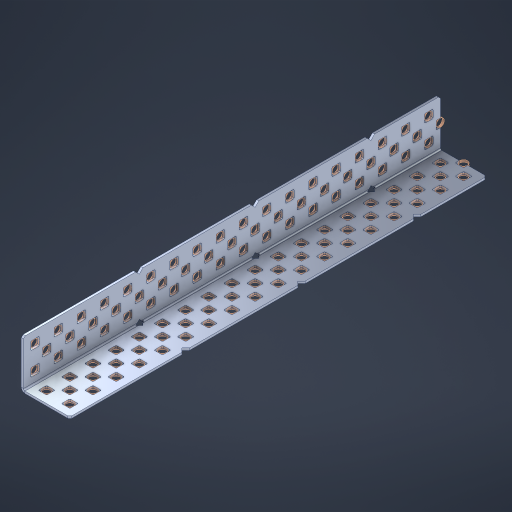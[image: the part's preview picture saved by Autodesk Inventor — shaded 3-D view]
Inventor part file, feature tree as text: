
AUTODESK INVENTOR PART (.ipt)
format: ipt  version: 2023 (Build 270158000, 158)  size: 1,412,096 bytes
history: native  units: in
note: dims shown in document units (in); Inventor stores cm internally (conversion verified against a paired STEP export)
features: other x114, extrude x106, sheet_metal_op x8, sketch x7, pattern_linear x2, mirror x1, chamfer x1
ambient origin geometry x8: Origin, YZ Plane, XZ Plane, XY Plane, X Axis, Y Axis, Z Axis, Center Point
bodies: Solid1 (feature_tree), Body (feature_tree)
feature tree (239):
  sheet_metal_op  "Flanges"
  sheet_metal_op  "Body Pattern"
  pattern_linear  "Center Pattern"  Spacing1=1.0in  [1 undecoded]
  other  "Arc Length"
  pattern_linear  "Notch Pattern"  Spacing1=0.1875in  [1 undecoded]
  other  "Diagonal Plane"
  mirror  "Everything Mirrored"
  chamfer  "End Chamfer"
  sketch  "Sketch1"  dims[d0=1.0in]
  other  "Plate1"
  sketch  "Sketch2"  dims[d1=9.0in]
  other  "Plate2"
  sheet_metal_op  "Bend1"
  sheet_metal_op  "Corner1"
  sketch  "Sketch8"  dims[d2=0.0469in]
  sketch  "Sketch9"  dims[d3=0.0469in]
  other  "Srf91"
  sheet_metal_op  "Body Pattern Sketch"
  other  "Srf92"
  sketch  "Sketch13"  dims[d4=0.0234in]
  sketch  "Sketch15"  dims[d5=0.0938in]
  sketch  "Sketch16"  dims[d6=0.0469in d7=1.0in d8=90.0deg d9=0.0312in d10=0.1875in d11=0.0469in d12=0.0469in d49=0.182in d50=0.02in d52=0.25in d53=0.0469in d54=0.0in d55=0.172in d56=1.0in d57=0.0in d60=7.0866in d62=0.5in d63=0.7874in d65=0.5in d85=0.1473in d86=0.1659in d89=0.0469in d90=0.0in d91=0.04in d92=0.0491in d95=2.5in d96=0.04in d97=0.25in d98=45.0deg d99=0.25in d106=0.182in d107=0.02in d108=0.5in d110=0.0469in d111=0.0in d112=0.172in d113=0.5in d114=0.0in d117=0.5in d123=0.25in d125=0.25in d126=0.0491in d127=0.1227in d128=0.08in d129=0.04in d130=2.5in]
  other  "Srf786"
  other  "Srf856"
  other  "Srf857"
  other  "Srf858"
  other  "Srf859"
  other  "Srf860"
  other  "Srf861"
  other  "Srf889"
  other  "Srf890"
  other  "Srf891"
  other  "Srf1275"
  other  "Srf1276"
  other  "Srf1278"
  other  "Srf1279"
  other  "Srf1280"
  other  "Srf1281"
  other  "Srf1282"
  other  "Srf1283"
  other  "Srf1277"
  other  "Srf1285"
  other  "Srf1286"
  other  "Srf1287"
  other  "Srf1383"
  other  "Srf1384"
  other  "Srf1385"
  other  "Srf1386"
  other  "Srf1387"
  other  "Srf1388"
  other  "Srf1389"
  other  "Srf1390"
  other  "Srf1391"
  other  "Srf1392"
  other  "Srf1393"
  other  "Srf1394"
  other  "Srf1395"
  other  "Srf1396"
  other  "Srf1397"
  other  "Srf1398"
  other  "Srf1399"
  other  "Srf1400"
  other  "Srf1401"
  other  "Srf1402"
  other  "Srf1403"
  other  "Srf1404"
  other  "Srf1405"
  other  "Srf1406"
  other  "Srf1407"
  other  "Srf1408"
  other  "Srf1409"
  other  "Srf1410"
  other  "Srf1445"
  other  "Srf1446"
  other  "Srf1447"
  other  "Srf1448"
  other  "Srf1449"
  other  "Srf1450"
  other  "Srf1451"
  other  "Srf1452"
  other  "Srf1453"
  other  "Srf1454"
  other  "Srf1455"
  other  "Srf1456"
  other  "Srf1457"
  other  "Srf1458"
  other  "Srf1475"
  other  "Srf1476"
  other  "Srf1477"
  other  "Srf1478"
  other  "Srf1479"
  other  "Srf1480"
  other  "Srf1481"
  other  "Srf1482"
  other  "Srf1483"
  other  "Srf1484"
  other  "Srf1485"
  other  "Srf1486"
  other  "Srf1487"
  other  "Srf1488"
  other  "Srf1489"
  other  "Srf1490"
  other  "Srf1491"
  other  "Srf1492"
  other  "Srf1493"
  other  "Srf1494"
  other  "Srf1495"
  other  "Srf1496"
  other  "Srf1497"
  other  "Srf1498"
  other  "Srf1499"
  other  "Srf1500"
  other  "Srf1501"
  other  "Srf1502"
  other  "Srf1537"
  other  "Srf1538"
  other  "Srf1539"
  other  "Srf1540"
  other  "Srf1541"
  other  "Srf1542"
  other  "Srf1543"
  other  "Srf1544"
  other  "Srf1545"
  other  "Srf1546"
  other  "Srf1547"
  other  "Srf1548"
  other  "Srf1549"
  other  "Srf1550"
  sheet_metal_op  "Body Stamp"
  sheet_metal_op  "Body Circle"
  other  "Center Stamp"
  other  "Center Circle"
  sheet_metal_op  "Notch"
  extrude  "ExtrusionSrf92"  Depth=0.0469in
  extrude  "ExtrusionSrf856"  Depth=0.0469in
  extrude  "ExtrusionSrf857"  Depth=0.182in
  extrude  "ExtrusionSrf858"  Depth=0.02in
  extrude  "ExtrusionSrf859"  Depth=0.25in
  extrude  "ExtrusionSrf860"  Depth=0.0469in
  extrude  "ExtrusionSrf861"  TaperAngle=0.0deg  [1 undecoded]
  extrude  "ExtrusionSrf889"  Depth=2.5in
  extrude  "ExtrusionSrf890"  Depth=1.0in TaperAngle=0.0deg
  extrude  "ExtrusionSrf891"  Depth=2.5in
  extrude  "ExtrusionSrf1275"  Depth=0.5in
  extrude  "ExtrusionSrf1276"  Depth=2.5in
  extrude  "ExtrusionSrf1277"  Depth=2.5in
  extrude  "ExtrusionSrf1278"  Depth=0.0469in
  extrude  "ExtrusionSrf1279"  Depth=2.5in TaperAngle=0.0deg
  extrude  "ExtrusionSrf1280"  Depth=2.5in
  extrude  "ExtrusionSrf1281"  Depth=0.25in TaperAngle=45.0deg
  extrude  "ExtrusionSrf1282"  Depth=0.25in
  extrude  "ExtrusionSrf1345"  Depth=0.182in
  extrude  "ExtrusionSrf1346"  Depth=0.02in
  extrude  "ExtrusionSrf1347"  Depth=0.5in
  extrude  "ExtrusionSrf1348"  Depth=0.0469in
  extrude  "ExtrusionSrf1383"  TaperAngle=0.0deg  [1 undecoded]
  extrude  "ExtrusionSrf1384"  Depth=2.5in
  extrude  "ExtrusionSrf1385"  Depth=0.5in TaperAngle=0.0deg
  extrude  "ExtrusionSrf1386"  Depth=0.5in
  extrude  "ExtrusionSrf1387"  Depth=0.25in
  extrude  "ExtrusionSrf1388"  Depth=0.25in
  extrude  "ExtrusionSrf1389"  Depth=2.5in
  extrude  "ExtrusionSrf1390"  Depth=2.5in
  extrude  "ExtrusionSrf1391"  Depth=2.5in
  extrude  "ExtrusionSrf1392"  Depth=2.5in
  extrude  "ExtrusionSrf1393"  Depth=2.5in
  extrude  "ExtrusionSrf1394"  [1 undecoded]
  extrude  "ExtrusionSrf1395"  [1 undecoded]
  extrude  "ExtrusionSrf1396"  [1 undecoded]
  extrude  "ExtrusionSrf1397"  [1 undecoded]
  extrude  "ExtrusionSrf1398"  [1 undecoded]
  extrude  "ExtrusionSrf1399"  [1 undecoded]
  extrude  "ExtrusionSrf1400"  [1 undecoded]
  extrude  "ExtrusionSrf1401"  [1 undecoded]
  extrude  "ExtrusionSrf1402"  [1 undecoded]
  extrude  "ExtrusionSrf1403"  [1 undecoded]
  extrude  "ExtrusionSrf1404"  [1 undecoded]
  extrude  "ExtrusionSrf1405"  [1 undecoded]
  extrude  "ExtrusionSrf1406"  [1 undecoded]
  extrude  "ExtrusionSrf1407"  [1 undecoded]
  extrude  "ExtrusionSrf1408"  [1 undecoded]
  extrude  "ExtrusionSrf1409"  [1 undecoded]
  extrude  "ExtrusionSrf1410"  [1 undecoded]
  extrude  "ExtrusionSrf1445"  [1 undecoded]
  extrude  "ExtrusionSrf1446"  [1 undecoded]
  extrude  "ExtrusionSrf1447"  [1 undecoded]
  extrude  "ExtrusionSrf1448"  [1 undecoded]
  extrude  "ExtrusionSrf1449"  [1 undecoded]
  extrude  "ExtrusionSrf1450"  [1 undecoded]
  extrude  "ExtrusionSrf1451"  [1 undecoded]
  extrude  "ExtrusionSrf1452"  [1 undecoded]
  extrude  "ExtrusionSrf1453"  [1 undecoded]
  extrude  "ExtrusionSrf1454"  [1 undecoded]
  extrude  "ExtrusionSrf1455"  [1 undecoded]
  extrude  "ExtrusionSrf1456"  [1 undecoded]
  extrude  "ExtrusionSrf1457"  [1 undecoded]
  extrude  "ExtrusionSrf1458"  [1 undecoded]
  extrude  "ExtrusionSrf1475"  [1 undecoded]
  extrude  "ExtrusionSrf1476"  [1 undecoded]
  extrude  "ExtrusionSrf1477"  [1 undecoded]
  extrude  "ExtrusionSrf1478"  [1 undecoded]
  extrude  "ExtrusionSrf1479"  [1 undecoded]
  extrude  "ExtrusionSrf1480"  [1 undecoded]
  extrude  "ExtrusionSrf1481"  [1 undecoded]
  extrude  "ExtrusionSrf1482"  [1 undecoded]
  extrude  "ExtrusionSrf1483"  [1 undecoded]
  extrude  "ExtrusionSrf1484"  [1 undecoded]
  extrude  "ExtrusionSrf1485"  [1 undecoded]
  extrude  "ExtrusionSrf1486"  [1 undecoded]
  extrude  "ExtrusionSrf1487"  [1 undecoded]
  extrude  "ExtrusionSrf1488"  [1 undecoded]
  extrude  "ExtrusionSrf1489"  [1 undecoded]
  extrude  "ExtrusionSrf1490"  [1 undecoded]
  extrude  "ExtrusionSrf1491"  [1 undecoded]
  extrude  "ExtrusionSrf1492"  [1 undecoded]
  extrude  "ExtrusionSrf1493"  [1 undecoded]
  extrude  "ExtrusionSrf1494"  [1 undecoded]
  extrude  "ExtrusionSrf1495"  [1 undecoded]
  extrude  "ExtrusionSrf1496"  [1 undecoded]
  extrude  "ExtrusionSrf1497"  [1 undecoded]
  extrude  "ExtrusionSrf1498"  [1 undecoded]
  extrude  "ExtrusionSrf1499"  [1 undecoded]
  extrude  "ExtrusionSrf1500"  [1 undecoded]
  extrude  "ExtrusionSrf1501"  [1 undecoded]
  extrude  "ExtrusionSrf1502"  [1 undecoded]
  extrude  "ExtrusionSrf1537"  [1 undecoded]
  extrude  "ExtrusionSrf1538"  [1 undecoded]
  extrude  "ExtrusionSrf1539"  [1 undecoded]
  extrude  "ExtrusionSrf1540"  [1 undecoded]
  extrude  "ExtrusionSrf1541"  [1 undecoded]
  extrude  "ExtrusionSrf1542"  [1 undecoded]
  extrude  "ExtrusionSrf1543"  [1 undecoded]
  extrude  "ExtrusionSrf1544"  [1 undecoded]
  extrude  "ExtrusionSrf1545"  [1 undecoded]
  extrude  "ExtrusionSrf1546"  [1 undecoded]
  extrude  "ExtrusionSrf1547"  [1 undecoded]
  extrude  "ExtrusionSrf1548"  [1 undecoded]
  extrude  "ExtrusionSrf1549"  [1 undecoded]
  extrude  "ExtrusionSrf1550"  [1 undecoded]
note: 77 required parameter values undecoded (feature->parameter linkage not recoverable at this tier; creation-order binding heuristic only, values carry confidence <= 0.55)
